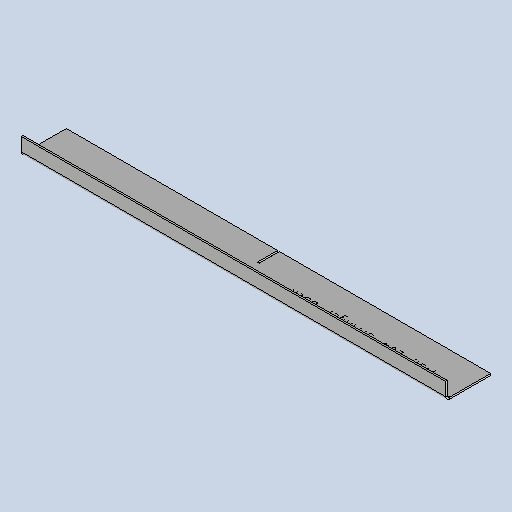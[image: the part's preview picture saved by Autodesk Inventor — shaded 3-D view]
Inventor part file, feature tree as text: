
AUTODESK INVENTOR PART (.ipt)
format: ipt  version: 2025 (Build 290162010, 162A)  size: 248,832 bytes
history: native  units: mm
features: other x5, sheet_metal_op x4, sketch x4, extrude x1
ambient origin geometry x8: Origin, YZ Plane, XZ Plane, XY Plane, X Axis, Y Axis, Z Axis, Center Point
bodies: Solid1 (feature_tree)
feature tree (14):
  sheet_metal_op  "Face1"
  sheet_metal_op  "Flange1"
  extrude  "Extrusion4"  Depth=52.0mm
  other  "Mark3"
  other  "A-Side Definition"
  sketch  "Sketch1"  dims[d0=980.0mm d1=52.0mm]
  other  "Plate1"
  sketch  "Sketch2"  dims[d2=2.0mm]
  other  "Plate2"
  sheet_metal_op  "Bend1"
  sheet_metal_op  "Corner1"
  sketch  "Sketch9"  dims[d3=2.0mm]
  sketch  "Sketch11"  dims[d4=1.0mm d5=4.0mm d6=2.75mm d7=20.0mm d8=90.0deg d9=2.75mm d10=8.0mm d11=2.0mm d12=2.75mm d38=200.0mm d39=12.0mm d44=60.0mm d45=0.0mm d46=0.0mm d47=2.1mm d49=490.0mm d50=29.0mm]
  other  "Definition1"
